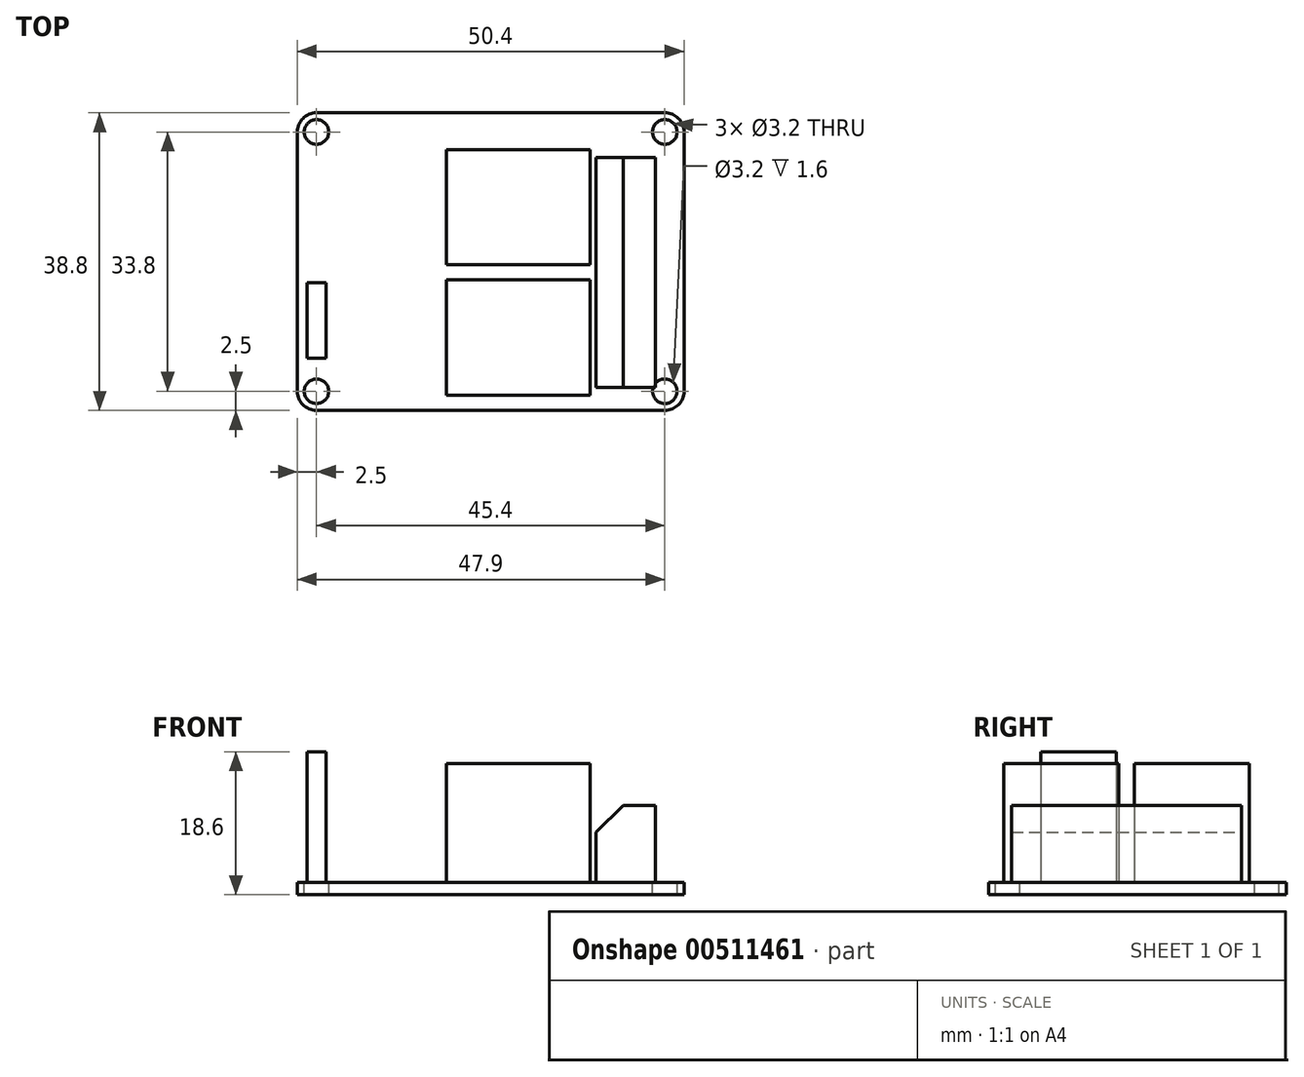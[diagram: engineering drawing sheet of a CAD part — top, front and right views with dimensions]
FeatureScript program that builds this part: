
annotation { "Feature Type Name" : "Feature", "Feature Type Description" : "" }
export const myFeature = defineFeature(function(context is Context, id is Id, definition is map)
    precondition{}
    {
        {
            var Q0;
            Q0=qCreatedBy(makeId("Top.planeOp"),FACE);
            var sketch = newSketch(context, id + "F0", { "sketchPlane" : qUnion([Q0])});
            skLineSegment(sketch, "E0.bottom", {"start": v(25.2, 19.4) * mm, "end": v(-25.2, 19.4) * mm});
            skLineSegment(sketch, "E0.top", {"start": v(25.2, -19.4) * mm, "end": v(-25.2, -19.4) * mm});
            skLineSegment(sketch, "E0.left", {"start": v(25.2, 19.4) * mm, "end": v(25.2, -19.4) * mm});
            skLineSegment(sketch, "E0.right", {"start": v(-25.2, 19.4) * mm, "end": v(-25.2, -19.4) * mm});
            skPoint(sketch, "E0.middle", {"position": v(0, 0) * mm});
            skSolve(sketch);
        }
        {
            var Q0;
            Q0=qSketchRegion(id+"F0",true);
            extrude(context, id + "F1", {"entities" : qUnion([Q0]), "depth" : 1.6 * mm, "offsetDistance" : 25 * mm});
        }
        {
            var Q0;
            Q0=makeQuery(id+"F1.opExtrude","CAP_FACE",FACE,{"disambiguationData":[OSD([sQuery(id+"F0.wireOp",EDGE,"E0.bottom"),sQuery(id+"F0.wireOp",EDGE,"E0.top"),sQuery(id+"F0.wireOp",EDGE,"E0.left"),sQuery(id+"F0.wireOp",EDGE,"E0.right")])],"isStart":false});
            var sketch = newSketch(context, id + "F2", { "sketchPlane" : qUnion([Q0])});
            skLineSegment(sketch, "E1.bottom", {"start": v(12.95, -17.4) * mm, "end": v(-5.8, -17.4) * mm});
            skLineSegment(sketch, "E1.top", {"start": v(12.95, -2.4) * mm, "end": v(-5.8, -2.4) * mm});
            skLineSegment(sketch, "E1.left", {"start": v(12.95, -17.4) * mm, "end": v(12.95, -2.4) * mm});
            skLineSegment(sketch, "E1.right", {"start": v(-5.8, -17.4) * mm, "end": v(-5.8, -2.4) * mm});
            skLineSegment(sketch, "E2.bottom", {"start": v(12.95, -0.4) * mm, "end": v(-5.8, -0.4) * mm});
            skLineSegment(sketch, "E2.top", {"start": v(12.95, 14.6) * mm, "end": v(-5.8, 14.6) * mm});
            skLineSegment(sketch, "E2.left", {"start": v(12.95, -0.4) * mm, "end": v(12.95, 14.6) * mm});
            skLineSegment(sketch, "E2.right", {"start": v(-5.8, -0.4) * mm, "end": v(-5.8, 14.6) * mm});
            skSolve(sketch);
        }
        {
            var Q0;
            Q0=qSketchRegion(id+"F2",true);
            extrude(context, id + "F3", {"entities" : qUnion([Q0]), "operationType" : NewBodyOperationType.ADD, "depth" : 15.5 * mm, "offsetDistance" : 25 * mm});
        }
        {
            var Q0;
            Q0=makeQuery(id+"F1.opExtrude","CAP_FACE",FACE,{"disambiguationData":[OSD([sQuery(id+"F0.wireOp",EDGE,"E0.bottom"),sQuery(id+"F0.wireOp",EDGE,"E0.top"),sQuery(id+"F0.wireOp",EDGE,"E0.left"),sQuery(id+"F0.wireOp",EDGE,"E0.right")])],"isStart":false});
            var sketch = newSketch(context, id + "F4", { "sketchPlane" : qUnion([Q0])});
            skLineSegment(sketch, "E3.bottom", {"start": v(13.75, 13.6) * mm, "end": v(21.5, 13.6) * mm});
            skLineSegment(sketch, "E3.top", {"start": v(13.75, -16.4) * mm, "end": v(21.5, -16.4) * mm});
            skLineSegment(sketch, "E3.left", {"start": v(13.75, 13.6) * mm, "end": v(13.75, -16.4) * mm});
            skLineSegment(sketch, "E3.right", {"start": v(21.5, 13.6) * mm, "end": v(21.5, -16.4) * mm});
            skPoint(sketch, "E4", {"position": v(17.62, -1.4) * mm});
            skPoint(sketch, "E4.positionSnap0", {"position": v(21.5, -1.4) * mm});
            skPoint(sketch, "E4.positionSnap1", {"position": v(17.62, 13.6) * mm});
            skSolve(sketch);
        }
        {
            var Q0;
            Q0=qSketchRegion(id+"F4",true);
            extrude(context, id + "F5", {"entities" : qUnion([Q0]), "operationType" : NewBodyOperationType.ADD, "depth" : 10 * mm, "offsetDistance" : 25 * mm});
        }
        {
            var Q0;
            Q0=makeQuery(id+"F5.opExtrude","CAP_EDGE",EDGE,{"disambiguationData":[OSD([sQuery(id+"F4.wireOp",EDGE,"E3.left")])],"isStart":false});
            chamfer(context, id + "F6", {"entities" : qUnion([Q0]), "chamferType" : ChamferType.OFFSET_ANGLE, "width" : 3.5 * mm, "oppositeDirection" : false, "angle" : 45 * degree, "tangentPropagation" : true});
        }
        {
            var Q0;
            Q0=makeQuery(id+"F1.opExtrude","CAP_FACE",FACE,{"disambiguationData":[OSD([sQuery(id+"F0.wireOp",EDGE,"E0.bottom"),sQuery(id+"F0.wireOp",EDGE,"E0.top"),sQuery(id+"F0.wireOp",EDGE,"E0.left"),sQuery(id+"F0.wireOp",EDGE,"E0.right")])],"isStart":false});
            var sketch = newSketch(context, id + "F7", { "sketchPlane" : qUnion([Q0])});
            skLineSegment(sketch, "E5.bottom", {"start": v(-23.95, -12.6) * mm, "end": v(-21.45, -12.6) * mm});
            skLineSegment(sketch, "E5.top", {"start": v(-23.95, -2.75) * mm, "end": v(-21.45, -2.75) * mm});
            skLineSegment(sketch, "E5.left", {"start": v(-23.95, -12.6) * mm, "end": v(-23.95, -2.75) * mm});
            skLineSegment(sketch, "E5.right", {"start": v(-21.45, -12.6) * mm, "end": v(-21.45, -2.75) * mm});
            skSolve(sketch);
        }
        {
            var Q0;
            Q0=qSketchRegion(id+"F7",true);
            extrude(context, id + "F8", {"entities" : qUnion([Q0]), "operationType" : NewBodyOperationType.ADD, "depth" : 17 * mm, "offsetDistance" : 25 * mm});
        }
        {
            var Q0;
            Q0=makeQuery(id+"F1.opExtrude","SWEPT_EDGE",EDGE,{"disambiguationData":[OSD([sQuery(id+"F0.wireOp",EDGE,"E0.bottom"),sQuery(id+"F0.wireOp",EDGE,"E0.right")])]});
            var Q1;
            Q1=makeQuery(id+"F1.opExtrude","SWEPT_EDGE",EDGE,{"disambiguationData":[OSD([sQuery(id+"F0.wireOp",EDGE,"E0.bottom"),sQuery(id+"F0.wireOp",EDGE,"E0.left")])]});
            var Q2;
            Q2=makeQuery(id+"F1.opExtrude","SWEPT_EDGE",EDGE,{"disambiguationData":[OSD([sQuery(id+"F0.wireOp",EDGE,"E0.top"),sQuery(id+"F0.wireOp",EDGE,"E0.left")])]});
            var Q3;
            Q3=makeQuery(id+"F1.opExtrude","SWEPT_EDGE",EDGE,{"disambiguationData":[OSD([sQuery(id+"F0.wireOp",EDGE,"E0.top"),sQuery(id+"F0.wireOp",EDGE,"E0.right")])]});
            fillet(context, id + "F9", {"entities" : qUnion([Q0, Q1, Q2, Q3]), "radius" : 2.5 * mm, "tangentPropagation" : true, "allowEdgeOverflow" : false});
        }
        {
            var Q0;
            Q0=makeQuery(id+"F1.opExtrude","CAP_FACE",FACE,{"disambiguationData":[OSD([sQuery(id+"F0.wireOp",EDGE,"E0.bottom"),sQuery(id+"F0.wireOp",EDGE,"E0.top"),sQuery(id+"F0.wireOp",EDGE,"E0.left"),sQuery(id+"F0.wireOp",EDGE,"E0.right")])],"isStart":false});
            var sketch = newSketch(context, id + "F10", { "sketchPlane" : qUnion([Q0])});
            skCircle(sketch, "E6", {"center": v(-22.7, 16.9) * mm, "radius": 1.6 * mm});
            skCircle(sketch, "E7", {"center": v(22.7, 16.9) * mm, "radius": 1.6 * mm});
            skCircle(sketch, "E8", {"center": v(22.7, -16.9) * mm, "radius": 1.6 * mm});
            skCircle(sketch, "E9", {"center": v(-22.7, -16.9) * mm, "radius": 1.6 * mm});
            skSolve(sketch);
        }
        {
            var Q0;
            Q0=qSketchRegion(id+"F10",true);
            extrude(context, id + "F11", {"entities" : qUnion([Q0]), "operationType" : NewBodyOperationType.REMOVE, "endBound" : BoundingType.THROUGH_ALL, "oppositeDirection" : true, "depth" : 25 * mm, "offsetDistance" : 25 * mm});
        }
    });
